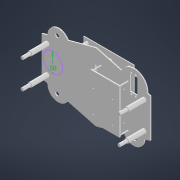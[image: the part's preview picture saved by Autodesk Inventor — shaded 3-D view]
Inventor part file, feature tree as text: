
AUTODESK INVENTOR PART (.ipt)
format: ipt  version: 2021 (Build 250183000, 183)  size: 256,512 bytes
history: native  units: in
note: dims shown in document units (in); Inventor stores cm internally (conversion verified against a paired STEP export)
features: reference x10, sketch x7, other x7, extrude x6, projected_geometry x3
ambient origin geometry x8: Origin, YZ Plane, XZ Plane, XY Plane, X Axis, Y Axis, Z Axis, Center Point
bodies: Solid2 (feature_tree), Solid3 (feature_tree), Solid1 (feature_tree)
feature tree (33):
  extrude  "Extrusion1"  Depth=0.3937in
  extrude  "Extrusion2"  Depth=0.1181in
  extrude  "Extrusion3"  Depth=0.1181in
  extrude  "Extrusion4"  Depth=0.9843in TaperAngle=0.0deg
  sketch  "Sketch7"  dims[d10=2.9528in d11=4.5276in]
  extrude  "Extrusion7"  Depth=4.5276in
  extrude  "Extrusion8"  TaperAngle=0.0deg  [1 undecoded]
  sketch  "Sketch1"  dims[d0=0.3937in d1=0.0in d2=2.7559in]
  reference  "Reference1"
  reference  "Reference2"
  reference  "Reference3"
  reference  "Reference4"
  sketch  "Sketch2"  dims[d3=4.3307in d4=0.1181in]
  reference  "Reference5"
  reference  "Reference6"
  sketch  "Sketch3"  dims[d5=0.1181in d6=0.1181in]
  sketch  "Sketch4"  dims[d7=0.1181in d8=0.9843in d9=0.0in]
  reference  "Reference7"
  reference  "Reference8"
  reference  "Reference9"
  reference  "Reference10"
  sketch  "Sketch8"  dims[d12=0.1181in d13=0.0in d14=0.0in d15=0.0in]
  sketch  "Sketch9"  dims[d27=1.9685in d28=2.874in d29=5.7087in d30=0.1181in d31=0.1181in d32=0.1181in d33=0.1181in d34=0.8661in d35=0.0in d36=3.0709in d37=5.9055in d38=0.1181in d39=0.0in]
  projected_geometry  "Projected Loop1"
  projected_geometry  "Projected Loop2"
  projected_geometry  "Projected Loop3"
  other  "Solid1:1"
  other  "<path> Marking Bot\Design\LMBOT V3 80%\iLMbot V3 75%.iam"
  other  "iLMbot V3 75%.iam"
  other  "Arduino Mega ATmega 2560:1"
  other  "Arduino Mega PCB_1"
  other  "RaspberryPi:1"
  other  "Mainboard2_1"
note: 1 required parameter value undecoded (feature->parameter linkage not recoverable at this tier; creation-order binding heuristic only, values carry confidence <= 0.55)
note: 1 file-system path scrubbed to <path> (originals preserved in map.json)
